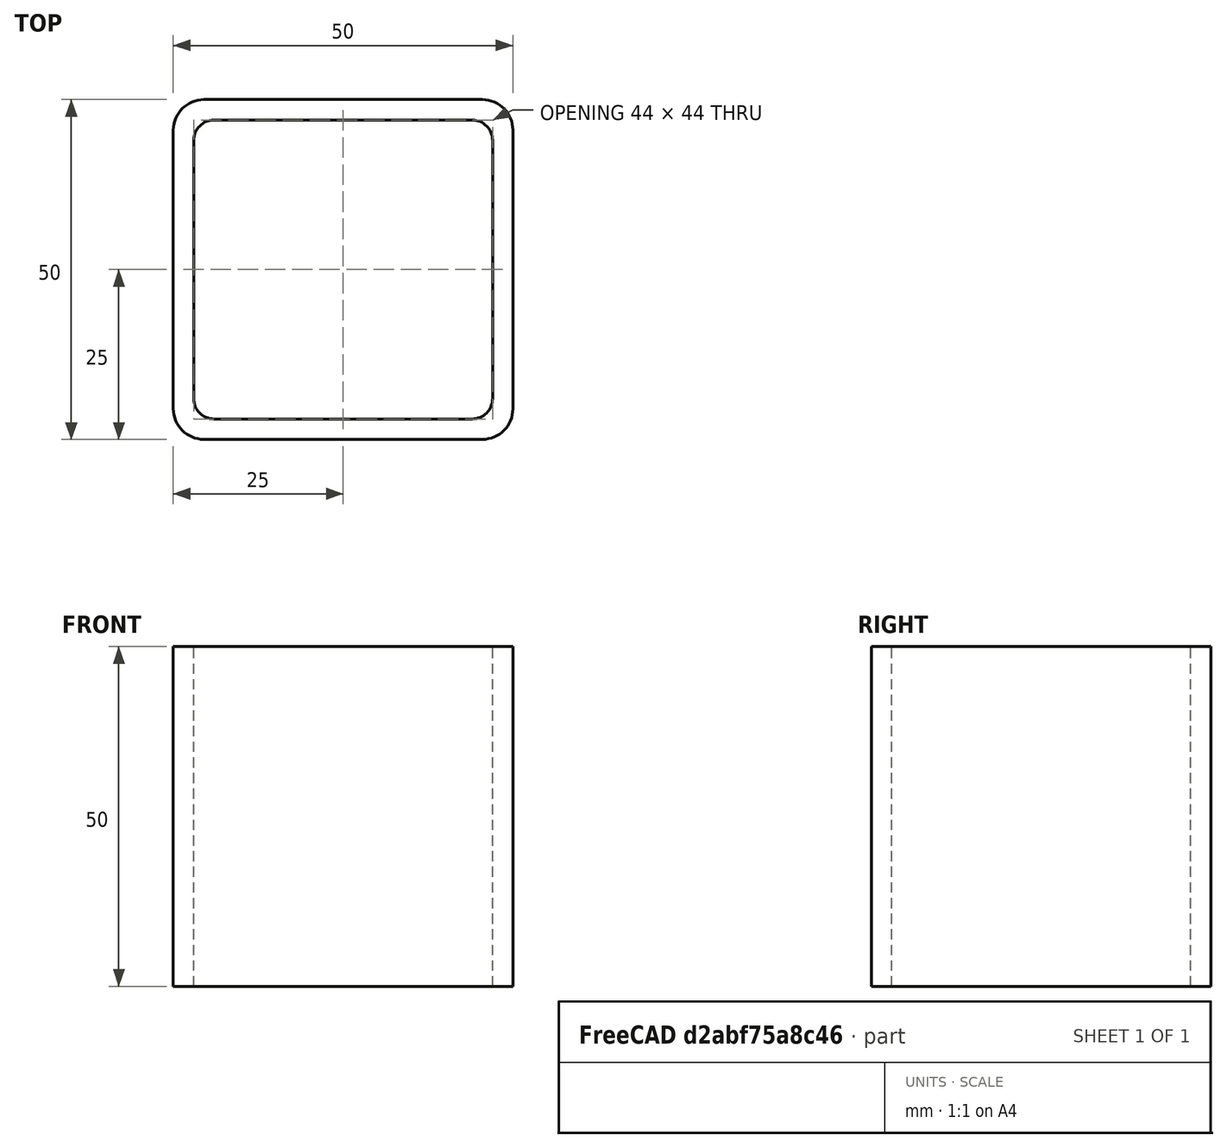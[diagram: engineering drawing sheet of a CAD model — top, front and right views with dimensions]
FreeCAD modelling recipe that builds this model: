
FCSTD DOCUMENT  (FreeCAD 0.15R4671 (Git))
Label: Square hollow section 50x50x3 EN10219 S235JRH
License: All rights reserved
LicenseURL: http://en.wikipedia.org/wiki/All_rights_reserved
objects: Sketcher::SketchObject×1, Part::Extrusion×1
note: 2 computed .brp shape members not serialized (recipe doc carries the construction recipe); baked Part::Feature solids carry a one-line shape summary decoded from their .brp

FEATURE [Sketcher::SketchObject] Sketch
  sketch-geometry (16):
    g0: LineSegment StartX=-19 StartY=22 StartZ=0 EndX=19 EndY=22 EndZ=0
    g1: LineSegment StartX=22 StartY=19 StartZ=0 EndX=22 EndY=-19 EndZ=0
    g2: LineSegment StartX=19 StartY=-22 StartZ=0 EndX=-19 EndY=-22 EndZ=0
    g3: LineSegment StartX=-22 StartY=-19 StartZ=0 EndX=-22 EndY=19 EndZ=0
    g4: LineSegment StartX=-20.5 StartY=25 StartZ=0 EndX=20.5 EndY=25 EndZ=0
    g5: LineSegment StartX=25 StartY=20.5 StartZ=0 EndX=25 EndY=-20.5 EndZ=0
    g6: LineSegment StartX=20.5 StartY=-25 StartZ=0 EndX=-20.5 EndY=-25 EndZ=0
    g7: LineSegment StartX=-25 StartY=-20.5 StartZ=0 EndX=-25 EndY=20.5 EndZ=0
    g8: ArcOfCircle CenterX=-19 CenterY=19 CenterZ=0 NormalX=0 NormalY=0 NormalZ=1 Radius=3 StartAngle=1.5708 EndAngle=3.14159
    g9: ArcOfCircle CenterX=19 CenterY=19 CenterZ=0 NormalX=0 NormalY=0 NormalZ=1 Radius=3 StartAngle=0 EndAngle=1.5708
    g10: ArcOfCircle CenterX=19 CenterY=-19 CenterZ=0 NormalX=0 NormalY=0 NormalZ=1 Radius=3 StartAngle=4.71239 EndAngle=6.28319
    g11: ArcOfCircle CenterX=-19 CenterY=-19 CenterZ=0 NormalX=0 NormalY=0 NormalZ=1 Radius=3 StartAngle=3.14159 EndAngle=4.71239
    g12: ArcOfCircle CenterX=20.5 CenterY=20.5 CenterZ=0 NormalX=0 NormalY=0 NormalZ=1 Radius=4.5 StartAngle=0 EndAngle=1.5708
    g13: ArcOfCircle CenterX=20.5 CenterY=-20.5 CenterZ=0 NormalX=0 NormalY=0 NormalZ=1 Radius=4.5 StartAngle=4.71239 EndAngle=6.28319
    g14: ArcOfCircle CenterX=-20.5 CenterY=-20.5 CenterZ=0 NormalX=0 NormalY=0 NormalZ=1 Radius=4.5 StartAngle=3.14159 EndAngle=4.71239
    g15: ArcOfCircle CenterX=-20.5 CenterY=20.5 CenterZ=0 NormalX=0 NormalY=0 NormalZ=1 Radius=4.5 StartAngle=1.5708 EndAngle=3.14159
  constraints (36):
    c: Horizontal(g2)
    c: Vertical(g3)
    c: Horizontal(g6)
    c: Vertical(g7)
    c: Tangent(g3,g8) = 1.5708
    c: Tangent(g0,g8) = 1.5708
    c: Tangent(g0,g9) = 1.5708
    c: Tangent(g1,g9) = 1.5708
    c: Tangent(g1,g10) = 1.5708
    c: Tangent(g2,g10) = 1.5708
    c: Tangent(g2,g11) = 1.5708
    c: Tangent(g3,g11) = 1.5708
    c: Tangent(g4,g12) = 1.5708
    c: Tangent(g5,g12) = 1.5708
    c: Tangent(g5,g13) = 1.5708
    c: Tangent(g6,g13) = 1.5708
    c: Tangent(g6,g14) = 1.5708
    c: Tangent(g7,g14) = 1.5708
    c: Tangent(g7,g15) = 1.5708
    c: Tangent(g4,g15) = 1.5708
    c: Equal(g9,g8)
    c: Equal(g9,g11)
    c: Equal(g9,g10)
    c: Equal(g12,g15)
    c: Equal(g12,g14)
    c: Equal(g12,g13)
    c: Symmetric(g4,g6,g-1)
    c: Symmetric(g7,g5,g-2)
    c: DistanceY(g4,g6) = -50
    c: DistanceX(g7,g5) = 50
    c: Symmetric(g3,g1,g-2)
    c: Symmetric(g0,g2,g-1)
    c: DistanceY(g0,g4) = 3
    c: DistanceX(g5,g1) = -3
    c: Radius(g9) = 3
    c: Radius(g12) = 4.5
FEATURE [Part::Extrusion] Extrude  label="Square hollow section 50x50x3 EN10219 S235JRH"
  Base = -> Sketch
  Dir = (0,0,50)
  Solid = true
